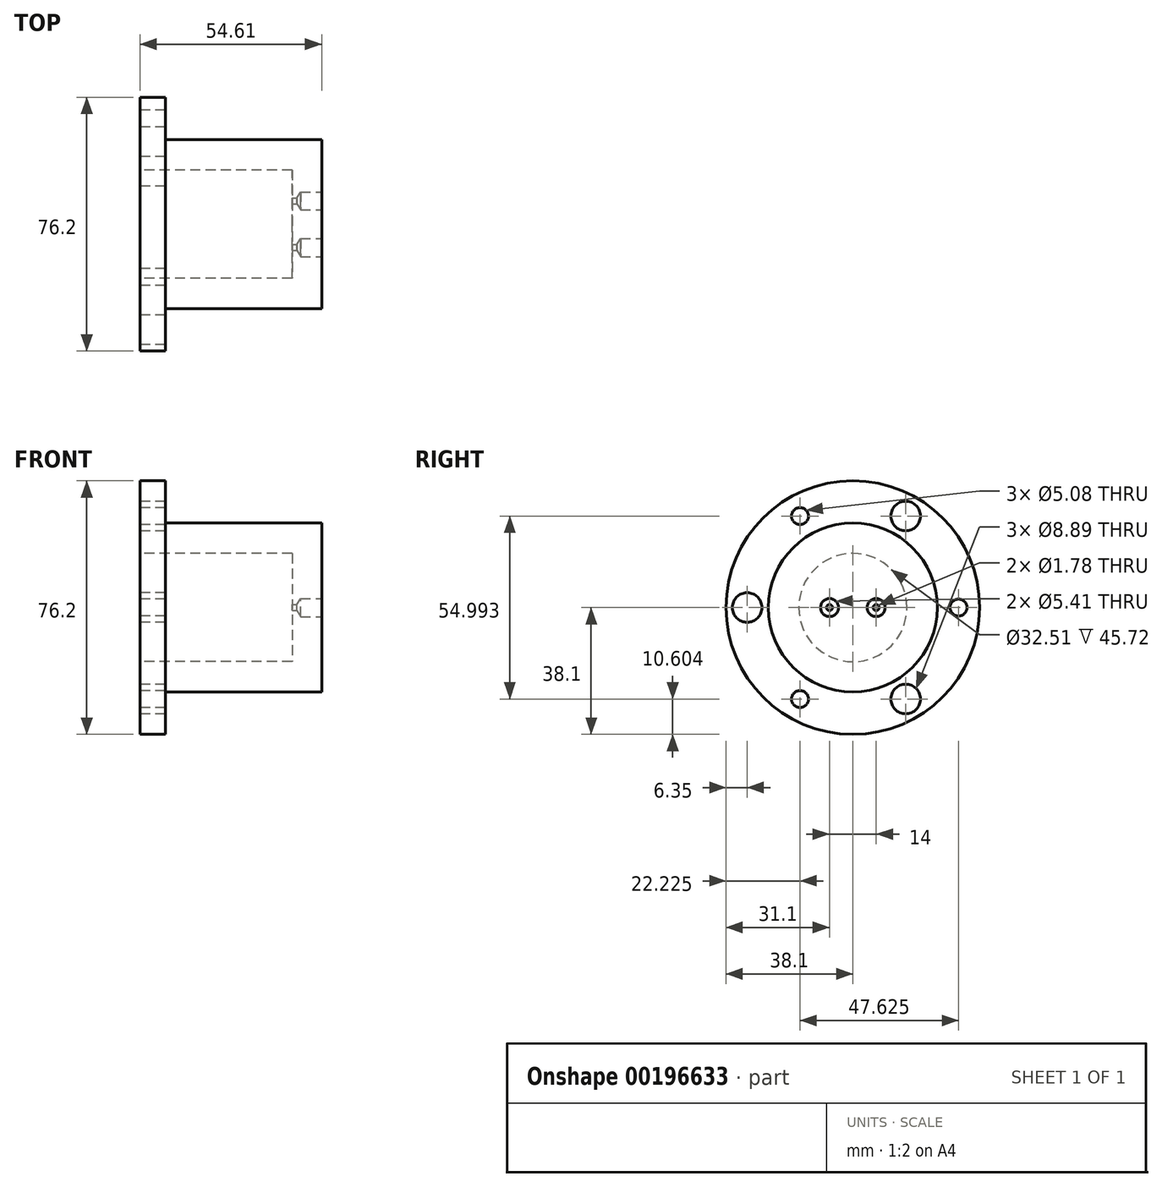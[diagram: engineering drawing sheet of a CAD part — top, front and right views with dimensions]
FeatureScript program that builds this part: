
annotation { "Feature Type Name" : "Feature", "Feature Type Description" : "" }
export const myFeature = defineFeature(function(context is Context, id is Id, definition is map)
    precondition{}
    {
        {
            var Q0;
            Q0=qCreatedBy(makeId("Front.planeOp"),FACE);
            var sketch = newSketch(context, id + "F0", { "sketchPlane" : qUnion([Q0])});
            skLineSegment(sketch, "E0.bottom", {"start": v(-19.05, -25.4) * mm, "end": v(19.05, -25.4) * mm});
            skLineSegment(sketch, "E0.top", {"start": v(-19.05, -16.26) * mm, "end": v(19.05, -16.26) * mm});
            skLineSegment(sketch, "E0.left", {"start": v(-19.05, -25.4) * mm, "end": v(-19.05, -16.26) * mm});
            skLineSegment(sketch, "E0.right", {"start": v(19.05, -25.4) * mm, "end": v(19.05, -16.26) * mm});
            skPoint(sketch, "E0.middle", {"position": v(0, -20.83) * mm});
            skSolve(sketch);
        }
        {
            var Q0;
            Q0=qCreatedBy(makeId("Front.planeOp"),FACE);
            var sketch = newSketch(context, id + "F1", { "sketchPlane" : qUnion([Q0])});
            skLineSegment(sketch, "E1", {"start": v(-54.66, 0) * mm, "end": v(61.53, 0) * mm});
            skSolve(sketch);
        }
        {
            var Q0;
            Q0 = qSketchRegion(id + "F0", true);
            var Q1;
            Q1=sQuery(id+"F1.wireOp",EDGE,"E1");
            revolve(context, id + "F2", {"entities" : qUnion([Q0]), "axis" : qUnion([Q1]), "revolveType" : RevolveType.FULL});
        }
        {
            var Q0;
            Q0=makeQuery(id+"F2.opRevolve","SWEPT_FACE",FACE,{"disambiguationData":[OSD([sQuery(id+"F0.wireOp",EDGE,"E0.right")])]});
            var sketch = newSketch(context, id + "F3", { "sketchPlane" : qUnion([Q0])});
            skCircle(sketch, "E2", {"center": v(0, 0) * mm, "radius": 25.4 * mm});
            skSolve(sketch);
        }
        {
            var Q0;
            Q0 = qSketchRegion(id + "F3", true);
            extrude(context, id + "F4", {"entities" : qUnion([Q0]), "operationType" : NewBodyOperationType.ADD, "depth" : 8.9 * mm});
        }
        {
            var Q0;
            Q0=qCreatedBy(makeId("Front.planeOp"),FACE);
            var sketch = newSketch(context, id + "F5", { "sketchPlane" : qUnion([Q0])});
            skLineSegment(sketch, "E3.bottom", {"start": v(-26.67, -38.1) * mm, "end": v(-19.05, -38.1) * mm});
            skLineSegment(sketch, "E3.top", {"start": v(-26.67, -16.26) * mm, "end": v(-19.05, -16.26) * mm});
            skLineSegment(sketch, "E3.left", {"start": v(-26.67, -38.1) * mm, "end": v(-26.67, -16.26) * mm});
            skLineSegment(sketch, "E3.right", {"start": v(-19.05, -38.1) * mm, "end": v(-19.05, -16.26) * mm});
            skPoint(sketch, "E3.middle", {"position": v(-22.86, -27.18) * mm});
            skSolve(sketch);
        }
        {
            var Q0;
            Q0=makeQuery(id+"F5.imprint","IMPRINT",FACE,{"disambiguationData":[TD([[makeQuery(id+"F5.imprint","IMPRINT",EDGE,{"derivedFrom":sQuery(id+"F5.wireOp",EDGE,"E3.bottom")}),1.0]])]});
            var Q1;
            Q1=sQuery(id+"F1.wireOp",EDGE,"E1");
            revolve(context, id + "F6", {"operationType" : NewBodyOperationType.ADD, "entities" : qUnion([Q0]), "axis" : qUnion([Q1]), "revolveType" : RevolveType.FULL});
        }
        {
            var Q0;
            Q0=makeQuery(id+"F6.opRevolve","SWEPT_FACE",FACE,{"disambiguationData":[OSD([sQuery(id+"F5.wireOp",EDGE,"E3.left")])]});
            var sketch = newSketch(context, id + "F7", { "sketchPlane" : qUnion([Q0])});
            skCircle(sketch, "E4", {"center": v(31.75, 0) * mm, "radius": 4.45 * mm});
            skCircle(sketch, "E5", {"center": v(15.88, 27.5) * mm, "radius": 2.54 * mm});
            skCircle(sketch, "E6", {"center": v(-15.88, 27.5) * mm, "radius": 4.45 * mm});
            skCircle(sketch, "E7", {"center": v(-31.75, 0) * mm, "radius": 2.54 * mm});
            skCircle(sketch, "E8", {"center": v(-15.88, -27.5) * mm, "radius": 4.45 * mm});
            skCircle(sketch, "E9", {"center": v(15.88, -27.5) * mm, "radius": 2.54 * mm});
            skSolve(sketch);
        }
        {
            var Q0;
            Q0 = qSketchRegion(id + "F7", true);
            var Q1;
            Q1=sQuery(id+"F7.wireOp",EDGE,"E4");
            extrude(context, id + "F8", {"entities" : qUnion([Q0]), "operationType" : NewBodyOperationType.REMOVE, "surfaceEntities" : qUnion([Q1]), "oppositeDirection" : true, "depth" : 7.62 * mm});
        }
        {
            var Q0;
            Q0=makeQuery(id+"F4.opExtrude","CAP_FACE",FACE,{"disambiguationData":[OSD([sQuery(id+"F3.wireOp",EDGE,"E2")])],"isStart":false});
            var sketch = newSketch(context, id + "F9", { "sketchPlane" : qUnion([Q0])});
            skPoint(sketch, "E10", {"position": v(-7, 0) * mm});
            skPoint(sketch, "E11", {"position": v(7, 0) * mm});
            skSolve(sketch);
        }
        {
            var Q0;
            Q0=sQuery(id+"F9.wireOp",VERTEX,"E10");
            var Q1;
            Q1=sQuery(id+"F9.wireOp",VERTEX,"E11");
            var Q2;
            Q2=makeQuery(id+"F2.opRevolve","SWEPT_BODY",BODY,{"disambiguationData":[OSD([sQuery(id+"F0.wireOp",EDGE,"E0.bottom"),sQuery(id+"F0.wireOp",EDGE,"E0.top"),sQuery(id+"F0.wireOp",EDGE,"E0.left"),sQuery(id+"F0.wireOp",EDGE,"E0.right")])]});
            hole(context, id + "F10", {"style" : HoleStyle.SIMPLE, "endStyle" : HoleEndStyle.BLIND, "holeDiameter" : 1.78 * mm, "holeDepth" : 8.9 * mm, "locations" : qUnion([Q0, Q1]), "scope" : qUnion([Q2])});
        }
        {
            var Q0;
            Q0=sQuery(id+"F9.wireOp",VERTEX,"E10");
            var Q1;
            Q1=sQuery(id+"F9.wireOp",VERTEX,"E11");
            var Q2;
            Q2=makeQuery(id+"F2.opRevolve","SWEPT_BODY",BODY,{"disambiguationData":[OSD([sQuery(id+"F0.wireOp",EDGE,"E0.bottom"),sQuery(id+"F0.wireOp",EDGE,"E0.top"),sQuery(id+"F0.wireOp",EDGE,"E0.left"),sQuery(id+"F0.wireOp",EDGE,"E0.right")])]});
            hole(context, id + "F11", {"style" : HoleStyle.SIMPLE, "endStyle" : HoleEndStyle.BLIND, "standardTappedOrClearance" : lookupTablePath({ "standard" : "ANSI", "engagement" : "75%", "pitch" : "28 tpi", "size" : "1/4", "type" : "Tapped" }), "standardBlindInLast" : lookupTablePath({ "standard" : "ANSI", "engagement" : "75%", "pitch" : "28 tpi", "size" : "1/4", "type" : "Tapped" }), "holeDiameter" : 5.4 * mm, "holeDepth" : 6.35 * mm, "locations" : qUnion([Q0, Q1]), "scope" : qUnion([Q2]), "majorDiameter" : 6.35 * mm});
        }
    });
